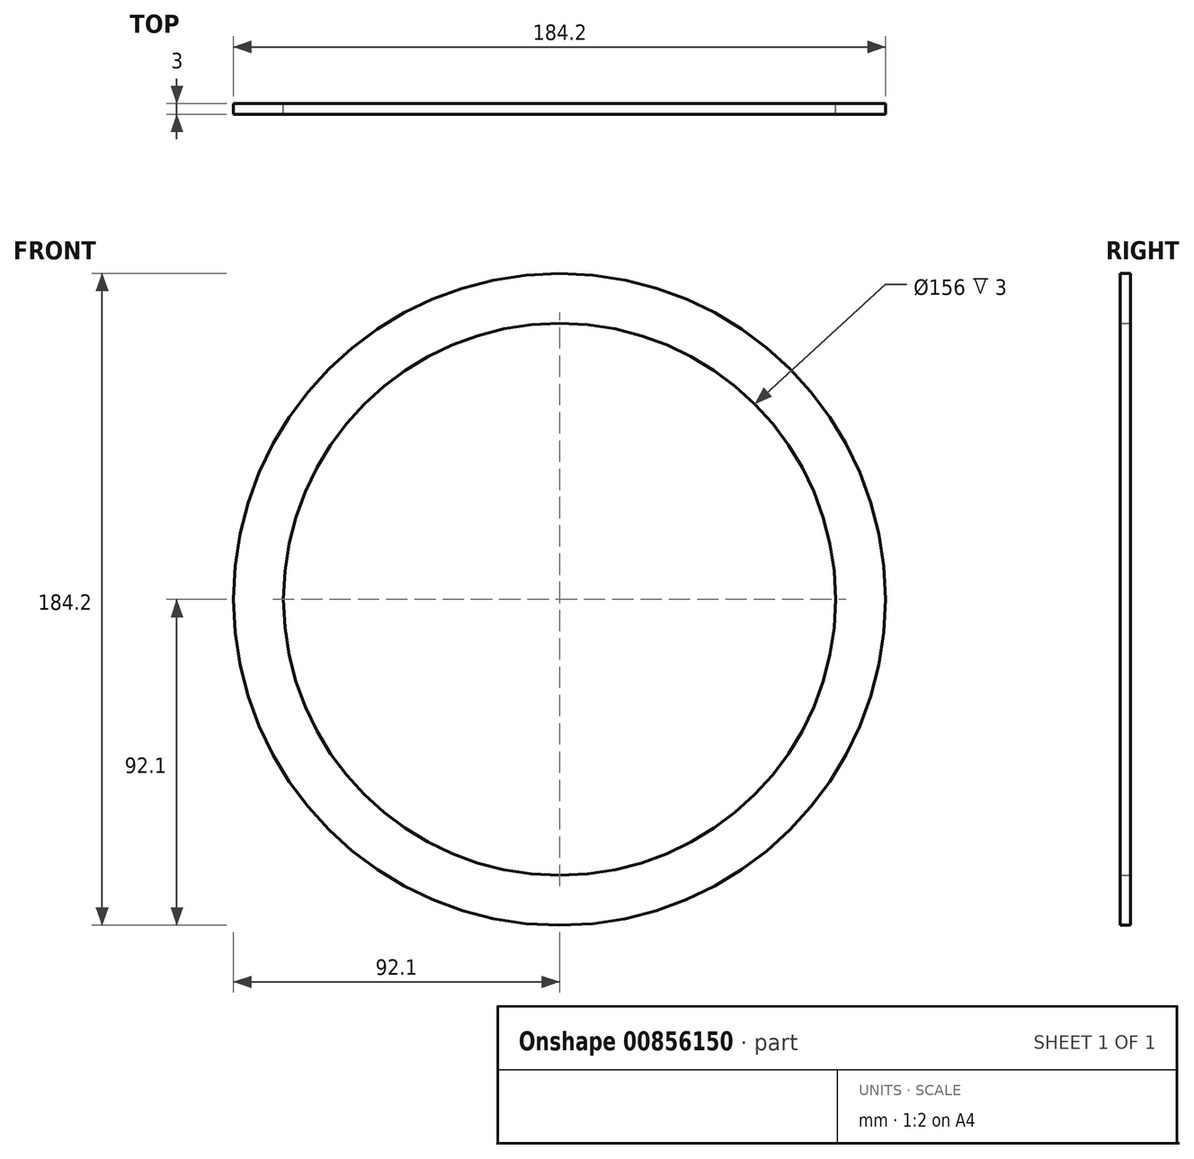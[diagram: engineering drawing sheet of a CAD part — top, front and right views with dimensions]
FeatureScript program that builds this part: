
annotation { "Feature Type Name" : "Feature", "Feature Type Description" : "" }
export const myFeature = defineFeature(function(context is Context, id is Id, definition is map)
    precondition{}
    {
        {
            var Q0;
            Q0=qCreatedBy(makeId("Front.planeOp"),FACE);
            var sketch = newSketch(context, id + "F0", { "sketchPlane" : qUnion([Q0])});
            skCircle(sketch, "E0", {"center": v(0, 0) * mm, "radius": 78 * mm});
            skCircle(sketch, "E1", {"center": v(0, 0) * mm, "radius": 92.1 * mm});
            skSolve(sketch);
        }
        {
            var Q0;
            Q0=makeQuery(id+"F0.imprint","IMPRINT",FACE,{"disambiguationData":[TD([[makeQuery(id+"F0.imprint","IMPRINT",EDGE,{"derivedFrom":sQuery(id+"F0.wireOp",EDGE,"E0")}),-1.0]])]});
            extrude(context, id + "F1", {"entities" : qUnion([Q0]), "depth" : 3 * mm, "offsetDistance" : 25 * mm});
        }
    });
